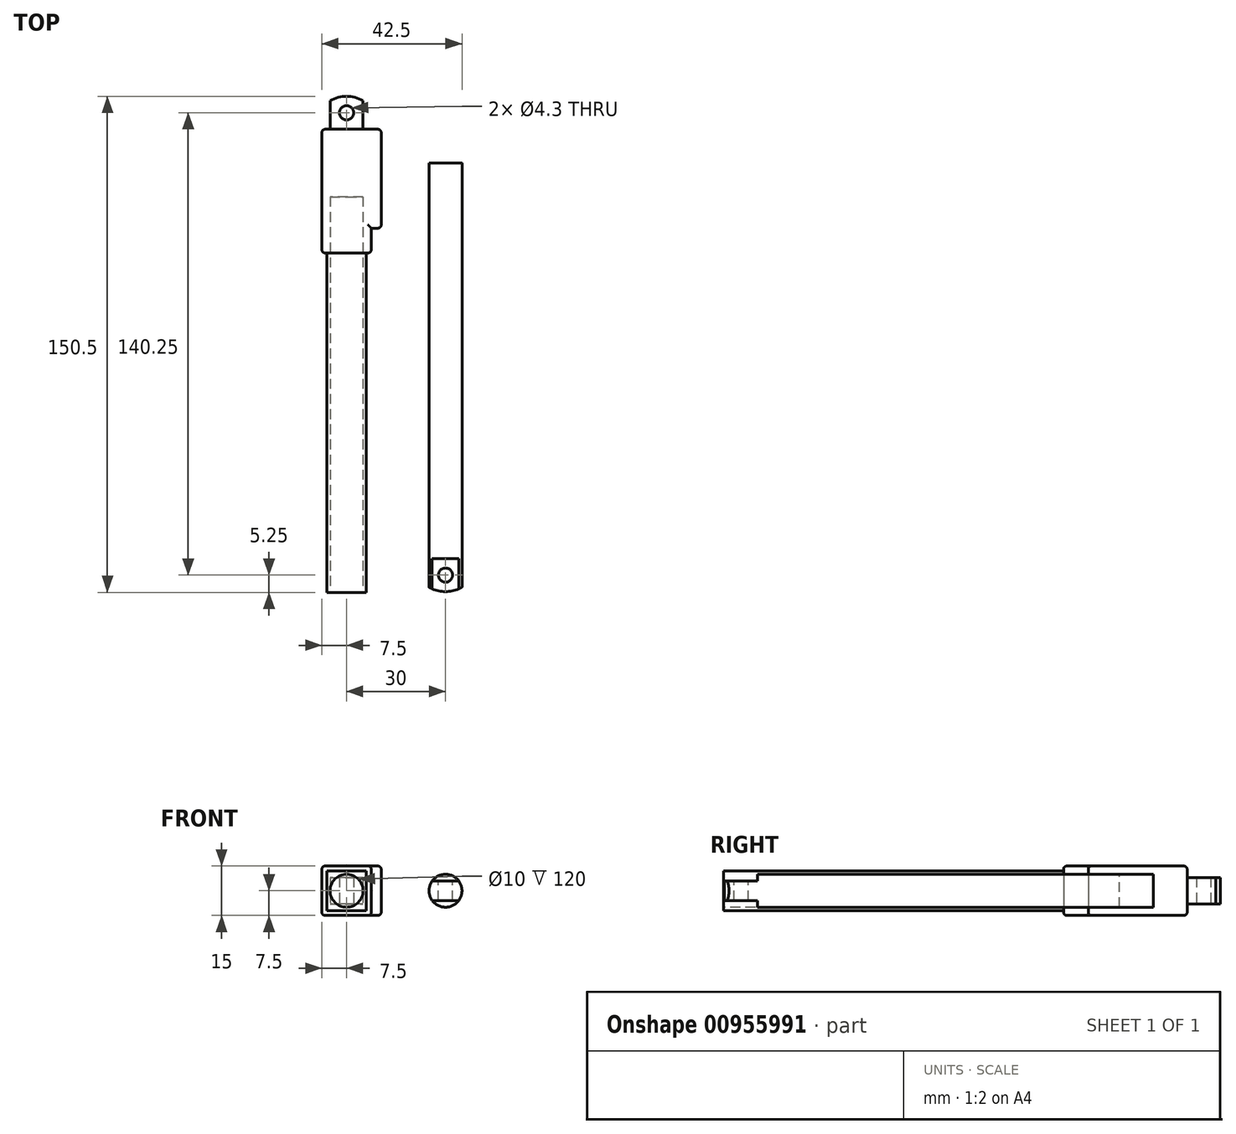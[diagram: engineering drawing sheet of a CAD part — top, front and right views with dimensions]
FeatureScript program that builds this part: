
annotation { "Feature Type Name" : "Feature", "Feature Type Description" : "" }
export const myFeature = defineFeature(function(context is Context, id is Id, definition is map)
    precondition{}
    {
        {
            var Q0;
            Q0=qCreatedBy(makeId("Top.planeOp"),FACE);
            var sketch = newSketch(context, id + "F0", { "sketchPlane" : qUnion([Q0])});
            skLineSegment(sketch, "E0.bottom", {"start": v(-6, -70.25) * mm, "end": v(6, -70.25) * mm});
            skLineSegment(sketch, "E0.top", {"start": v(-6, 70.25) * mm, "end": v(6, 70.25) * mm});
            skLineSegment(sketch, "E0.left", {"start": v(-6, -70.25) * mm, "end": v(-6, 70.25) * mm});
            skLineSegment(sketch, "E0.right", {"start": v(6, -70.25) * mm, "end": v(6, 70.25) * mm});
            skPoint(sketch, "E0.middle", {"position": v(0, 0) * mm});
            skLineSegment(sketch, "E1.bottom", {"start": v(-5, 70.25) * mm, "end": v(5, 70.25) * mm});
            skLineSegment(sketch, "E1.top", {"start": v(-5, 80.25) * mm, "end": v(5, 80.25) * mm});
            skLineSegment(sketch, "E1.left", {"start": v(-5, 70.25) * mm, "end": v(-5, 80.25) * mm});
            skLineSegment(sketch, "E1.right", {"start": v(5, 70.25) * mm, "end": v(5, 80.25) * mm});
            skCircle(sketch, "E2", {"center": v(0, 75.25) * mm, "radius": 2.15 * mm});
            skPoint(sketch, "E2.centerSnap0", {"position": v(-5, 75.25) * mm});
            skLineSegment(sketch, "E3.bottom", {"start": v(-7.5, 70.25) * mm, "end": v(7.5, 70.25) * mm});
            skLineSegment(sketch, "E3.top", {"start": v(-7.5, 32.75) * mm, "end": v(7.5, 32.75) * mm});
            skLineSegment(sketch, "E3.left", {"start": v(-7.5, 70.25) * mm, "end": v(-7.5, 32.75) * mm});
            skLineSegment(sketch, "E3.right", {"start": v(7.5, 70.25) * mm, "end": v(7.5, 32.75) * mm});
            skPoint(sketch, "E3.middle", {"position": v(0, 51.5) * mm});
            skLineSegment(sketch, "E4.bottom", {"start": v(7.5, 70.25) * mm, "end": v(10.5, 70.25) * mm});
            skLineSegment(sketch, "E4.top", {"start": v(7.5, 40.25) * mm, "end": v(10.5, 40.25) * mm});
            skLineSegment(sketch, "E4.left", {"start": v(7.5, 70.25) * mm, "end": v(7.5, 40.25) * mm});
            skLineSegment(sketch, "E4.right", {"start": v(10.5, 70.25) * mm, "end": v(10.5, 40.25) * mm});
            skCircle(sketch, "E5", {"center": v(0, 70.25) * mm, "radius": 10 * mm});
            skSolve(sketch);
        }
        {
            var Q0;
            Q0=makeQuery(id+"F0.imprint","IMPRINT",FACE,{"disambiguationData":[TD([[makeQuery(id+"F0.imprint","IMPRINT",EDGE,{"derivedFrom":sQuery(id+"F0.wireOp",EDGE,"E0.bottom")}),1.0]])]});
            var Q1;
            {var subQ0=sQuery(id+"F0.wireOp",EDGE,"E3.bottom");var subQ3=sQuery(id+"F0.wireOp",EDGE,"E0.left");var subQ4=makeQuery(id+"F0.imprint","INTERSECT",VERTEX,{"derivedFrom":[subQ3,subQ0]});Q1=makeQuery(id+"F0.imprint","IMPRINT",FACE,{"disambiguationData":[TD([[makeQuery(id+"F0.imprint","IMPRINT",EDGE,{"disambiguationData":[TD([[subQ4,1.0]])],"derivedFrom":subQ3}),-1.0]])]});}
            extrude(context, id + "F1", {"entities" : qUnion([Q0, Q1]), "depth" : 12 * mm, "offsetDistance" : 25 * mm, "symmetric" : true});
        }
        {
            var Q0;
            Q0=makeQuery(id+"F1.opExtrude","SWEPT_FACE",FACE,{"disambiguationData":[OSD([sQuery(id+"F0.wireOp",EDGE,"E0.bottom")])]});
            var sketch = newSketch(context, id + "F2", { "sketchPlane" : qUnion([Q0])});
            skLineSegment(sketch, "E6.bottom", {"start": v(-5, 5) * mm, "end": v(5, 5) * mm});
            skLineSegment(sketch, "E6.top", {"start": v(-5, -5) * mm, "end": v(5, -5) * mm});
            skLineSegment(sketch, "E6.left", {"start": v(-5, 5) * mm, "end": v(-5, -5) * mm});
            skLineSegment(sketch, "E6.right", {"start": v(5, 5) * mm, "end": v(5, -5) * mm});
            skPoint(sketch, "E6.middle", {"position": v(0, 0) * mm});
            skCircle(sketch, "E7", {"center": v(0, 0) * mm, "radius": 5 * mm});
            skSolve(sketch);
        }
        {
            var Q0;
            Q0=makeQuery(id+"F0.imprint","IMPRINT",FACE,{"disambiguationData":[TD([[makeQuery(id+"F0.imprint","IMPRINT",EDGE,{"derivedFrom":sQuery(id+"F0.wireOp",EDGE,"E4.bottom")}),-1.0]])]});
            var Q1;
            {var subQ0=sQuery(id+"F0.wireOp",EDGE,"E3.right");Q1=makeQuery(id+"F0.imprint","IMPRINT",FACE,{"disambiguationData":[TD([[makeQuery(id+"F0.imprint","IMPRINT",EDGE,{"derivedFrom":subQ0}),-1.0]])]});}
            var Q2;
            {var subQ5=sQuery(id+"F0.wireOp",EDGE,"E3.left");Q2=makeQuery(id+"F0.imprint","IMPRINT",FACE,{"disambiguationData":[TD([[makeQuery(id+"F0.imprint","IMPRINT",EDGE,{"derivedFrom":subQ5}),1.0]])]});}
            var Q3;
            {var subQ0=sQuery(id+"F0.wireOp",EDGE,"E3.bottom");var subQ3=sQuery(id+"F0.wireOp",EDGE,"E0.left");var subQ4=makeQuery(id+"F0.imprint","INTERSECT",VERTEX,{"derivedFrom":[subQ3,subQ0]});Q3=makeQuery(id+"F0.imprint","IMPRINT",FACE,{"disambiguationData":[TD([[makeQuery(id+"F0.imprint","IMPRINT",EDGE,{"disambiguationData":[TD([[subQ4,1.0]])],"derivedFrom":subQ3}),-1.0]])]});}
            var Q4;
            {var subQ0=sQuery(id+"F0.wireOp",EDGE,"E3.top");var subQ1=sQuery(id+"F0.wireOp",EDGE,"E0.left");var subQ2=makeQuery(id+"F0.imprint","INTERSECT",VERTEX,{"derivedFrom":[subQ1,subQ0]});Q4=makeQuery(id+"F0.imprint","IMPRINT",FACE,{"disambiguationData":[TD([[makeQuery(id+"F0.imprint","IMPRINT",EDGE,{"disambiguationData":[TD([[subQ2,-1.0]])],"derivedFrom":subQ1}),-1.0]])]});}
            var Q5;
            {var subQ2=sQuery(id+"F0.wireOp",EDGE,"E4.top");Q5=makeQuery(id+"F0.imprint","IMPRINT",FACE,{"disambiguationData":[TD([[makeQuery(id+"F0.imprint","IMPRINT",EDGE,{"derivedFrom":subQ2}),1.0]])]});}
            var Q6;
            {var subQ0=sQuery(id+"F0.wireOp",EDGE,"E3.bottom");var subQ1=sQuery(id+"F0.wireOp",EDGE,"E0.right");var subQ2=makeQuery(id+"F0.imprint","INTERSECT",VERTEX,{"derivedFrom":[subQ1,subQ0]});Q6=makeQuery(id+"F0.imprint","IMPRINT",FACE,{"disambiguationData":[TD([[makeQuery(id+"F0.imprint","IMPRINT",EDGE,{"disambiguationData":[TD([[subQ2,1.0]])],"derivedFrom":subQ1}),-1.0]])]});}
            extrude(context, id + "F3", {"entities" : qUnion([Q0, Q1, Q2, Q3, Q4, Q5, Q6]), "operationType" : NewBodyOperationType.ADD, "depth" : 15 * mm, "offsetDistance" : 25 * mm, "symmetric" : true});
        }
        {
            var Q0;
            {var subQ0=sQuery(id+"F2.wireOp",EDGE,"E7");var subQ1=makeQuery(id+"F2.imprint","INTERSECT",VERTEX,{"derivedFrom":[sQuery(id+"F2.wireOp",EDGE,"E6.bottom"),subQ0]});Q0=makeQuery(id+"F2.imprint","IMPRINT",FACE,{"disambiguationData":[TD([[makeQuery(id+"F2.imprint","IMPRINT",EDGE,{"disambiguationData":[TD([[subQ1,1.0]])],"derivedFrom":subQ0}),1.0]])]});}
            extrude(context, id + "F4", {"entities" : qUnion([Q0]), "operationType" : NewBodyOperationType.REMOVE, "oppositeDirection" : true, "depth" : 120 * mm, "offsetDistance" : 25 * mm});
        }
        {
            var Q0;
            Q0=qCreatedBy(makeId("Front.planeOp"),FACE);
            var sketch = newSketch(context, id + "F5", { "sketchPlane" : qUnion([Q0])});
            skCircle(sketch, "E8", {"center": v(30, 0) * mm, "radius": 5 * mm});
            skSolve(sketch);
        }
        {
            var Q0;
            Q0 = qSketchRegion(id + "F5", true);
            extrude(context, id + "F6", {"entities" : qUnion([Q0]), "depth" : 120 * mm, "offsetDistance" : 25 * mm, "symmetric" : true});
        }
        {
            var Q0;
            Q0=makeQuery(id+"F6.opExtrude","CAP_FACE",FACE,{"disambiguationData":[OSD([sQuery(id+"F5.wireOp",EDGE,"E8")])],"isStart":false});
            var sketch = newSketch(context, id + "F7", { "sketchPlane" : qUnion([Q0])});
            skLineSegment(sketch, "E9.bottom", {"start": v(25.96, 2.95) * mm, "end": v(34.04, 2.95) * mm});
            skLineSegment(sketch, "E9.top", {"start": v(25.96, -2.95) * mm, "end": v(34.04, -2.95) * mm});
            skLineSegment(sketch, "E9.left", {"start": v(25.96, 2.95) * mm, "end": v(25.96, -2.95) * mm});
            skLineSegment(sketch, "E9.right", {"start": v(34.04, 2.95) * mm, "end": v(34.04, -2.95) * mm});
            skPoint(sketch, "E9.middle", {"position": v(30, 0) * mm});
            skSolve(sketch);
        }
        {
            var Q0;
            {var subQ0=sQuery(id+"F7.wireOp",EDGE,"E9.left");Q0=makeQuery(id+"F7.imprint","IMPRINT",FACE,{"disambiguationData":[TD([[makeQuery(id+"F7.imprint","IMPRINT",EDGE,{"derivedFrom":subQ0}),-1.0]])]});}
            var Q1;
            Q1=makeQuery(id+"F7.imprint","IMPRINT",FACE,{"disambiguationData":[TD([[makeQuery(id+"F7.imprint","IMPRINT",EDGE,{"derivedFrom":sQuery(id+"F7.wireOp",EDGE,"E9.bottom")}),-1.0]])]});
            var Q2;
            {var subQ0=sQuery(id+"F7.wireOp",EDGE,"E9.right");Q2=makeQuery(id+"F7.imprint","IMPRINT",FACE,{"disambiguationData":[TD([[makeQuery(id+"F7.imprint","IMPRINT",EDGE,{"derivedFrom":subQ0}),1.0]])]});}
            extrude(context, id + "F8", {"entities" : qUnion([Q0, Q1, Q2]), "operationType" : NewBodyOperationType.ADD, "depth" : 10 * mm, "offsetDistance" : 25 * mm});
        }
        {
            var Q0;
            Q0=makeQuery(id+"F8.opExtrude","SWEPT_FACE",FACE,{"disambiguationData":[OSD([sQuery(id+"F7.wireOp",EDGE,"E9.bottom")])]});
            var sketch = newSketch(context, id + "F9", { "sketchPlane" : qUnion([Q0])});
            skCircle(sketch, "E10", {"center": v(30, -65) * mm, "radius": 2.15 * mm});
            skPoint(sketch, "E10.centerSnap0", {"position": v(30, -70) * mm});
            skPoint(sketch, "E10.centerSnap1", {"position": v(25.96, -65) * mm});
            skCircle(sketch, "E11", {"center": v(30, -60) * mm, "radius": 10 * mm});
            skLineSegment(sketch, "E12", {"start": v(25, -70) * mm, "end": v(35, -70) * mm});
            skLineSegment(sketch, "E13", {"start": v(35, -70) * mm, "end": v(35, -68.66) * mm});
            skLineSegment(sketch, "E14", {"start": v(25, -70) * mm, "end": v(25, -68.66) * mm});
            skSolve(sketch);
        }
        {
            var Q0;
            Q0=makeQuery(id+"F9.imprint","IMPRINT",FACE,{"disambiguationData":[TD([[makeQuery(id+"F9.imprint","IMPRINT",EDGE,{"derivedFrom":sQuery(id+"F9.wireOp",EDGE,"E10")}),1.0]])]});
            var Q1;
            {var subQ0=sQuery(id+"F9.wireOp",EDGE,"E12");var subQ1=sQuery(id+"F9.wireOp",EDGE,"E11");var subQ2=makeQuery(id+"F9.imprint","INTERSECT",VERTEX,{"derivedFrom":[subQ1,subQ0]});Q1=makeQuery(id+"F9.imprint","IMPRINT",FACE,{"disambiguationData":[TD([[makeQuery(id+"F9.imprint","IMPRINT",EDGE,{"disambiguationData":[TD([[subQ2,1.0]])],"derivedFrom":subQ1}),-1.0]])]});}
            var Q2;
            {var subQ0=sQuery(id+"F9.wireOp",EDGE,"E14");Q2=makeQuery(id+"F9.imprint","IMPRINT",FACE,{"disambiguationData":[TD([[makeQuery(id+"F9.imprint","IMPRINT",EDGE,{"derivedFrom":subQ0}),-1.0]])]});}
            var Q3;
            {var subQ0=sQuery(id+"F9.wireOp",EDGE,"E12");var subQ1=sQuery(id+"F9.wireOp",EDGE,"E11");var subQ2=makeQuery(id+"F9.imprint","INTERSECT",VERTEX,{"derivedFrom":[subQ1,subQ0]});Q3=makeQuery(id+"F9.imprint","IMPRINT",FACE,{"disambiguationData":[TD([[makeQuery(id+"F9.imprint","IMPRINT",EDGE,{"disambiguationData":[TD([[subQ2,-1.0]])],"derivedFrom":subQ1}),-1.0]])]});}
            var Q4;
            {var subQ0=sQuery(id+"F9.wireOp",EDGE,"E13");Q4=makeQuery(id+"F9.imprint","IMPRINT",FACE,{"disambiguationData":[TD([[makeQuery(id+"F9.imprint","IMPRINT",EDGE,{"derivedFrom":subQ0}),1.0]])]});}
            extrude(context, id + "F10", {"entities" : qUnion([Q0, Q1, Q2, Q3, Q4]), "operationType" : NewBodyOperationType.REMOVE, "oppositeDirection" : true, "depth" : 25 * mm, "offsetDistance" : 25 * mm});
        }
        {
            var Q0;
            Q0=makeQuery(id+"F0.imprint","IMPRINT",FACE,{"disambiguationData":[TD([[makeQuery(id+"F0.imprint","IMPRINT",EDGE,{"derivedFrom":sQuery(id+"F0.wireOp",EDGE,"E2")}),-1.0]])]});
            extrude(context, id + "F11", {"entities" : qUnion([Q0]), "operationType" : NewBodyOperationType.ADD, "depth" : 8 * mm, "offsetDistance" : 25 * mm, "symmetric" : true});
        }
        {
            var Q0;
            Q0=makeQuery(id+"F3.opExtrude","CAP_FACE",FACE,{"disambiguationData":[OSD([sQuery(id+"F0.wireOp",EDGE,"E3.bottom"),sQuery(id+"F0.wireOp",EDGE,"E3.top"),sQuery(id+"F0.wireOp",EDGE,"E3.left"),sQuery(id+"F0.wireOp",EDGE,"E3.right"),sQuery(id+"F0.wireOp",EDGE,"E4.bottom"),sQuery(id+"F0.wireOp",EDGE,"E4.top"),sQuery(id+"F0.wireOp",EDGE,"E4.right")])],"isStart":false});
            var Q1;
            Q1=makeQuery(id+"F3.opExtrude","CAP_FACE",FACE,{"disambiguationData":[OSD([sQuery(id+"F0.wireOp",EDGE,"E3.bottom"),sQuery(id+"F0.wireOp",EDGE,"E3.top"),sQuery(id+"F0.wireOp",EDGE,"E3.left"),sQuery(id+"F0.wireOp",EDGE,"E3.right"),sQuery(id+"F0.wireOp",EDGE,"E4.bottom"),sQuery(id+"F0.wireOp",EDGE,"E4.top"),sQuery(id+"F0.wireOp",EDGE,"E4.right")])],"isStart":true});
            var Q2;
            Q2=makeQuery(id+"F3.opExtrude","SWEPT_EDGE",EDGE,{"disambiguationData":[OSD([sQuery(id+"F0.wireOp",EDGE,"E3.top"),sQuery(id+"F0.wireOp",EDGE,"E3.left")])]});
            var Q3;
            Q3=makeQuery(id+"F3.opExtrude","SWEPT_EDGE",EDGE,{"disambiguationData":[OSD([sQuery(id+"F0.wireOp",EDGE,"E3.top"),sQuery(id+"F0.wireOp",EDGE,"E3.right")])]});
            var Q4;
            Q4=makeQuery(id+"F3.opExtrude","SWEPT_EDGE",EDGE,{"disambiguationData":[OSD([sQuery(id+"F0.wireOp",EDGE,"E4.top"),sQuery(id+"F0.wireOp",EDGE,"E4.right")])]});
            var Q5;
            Q5=makeQuery(id+"F3.opExtrude","SWEPT_EDGE",EDGE,{"disambiguationData":[OSD([sQuery(id+"F0.wireOp",EDGE,"E4.bottom"),sQuery(id+"F0.wireOp",EDGE,"E4.right")])]});
            var Q6;
            Q6=makeQuery(id+"F3.opExtrude","SWEPT_EDGE",EDGE,{"disambiguationData":[OSD([sQuery(id+"F0.wireOp",EDGE,"E3.bottom"),sQuery(id+"F0.wireOp",EDGE,"E3.left")])]});
            fillet(context, id + "F12", {"entities" : qUnion([Q0, Q1, Q2, Q3, Q4, Q5, Q6]), "radius" : 1 * mm, "tangentPropagation" : true, "allowEdgeOverflow" : false});
        }
    });
